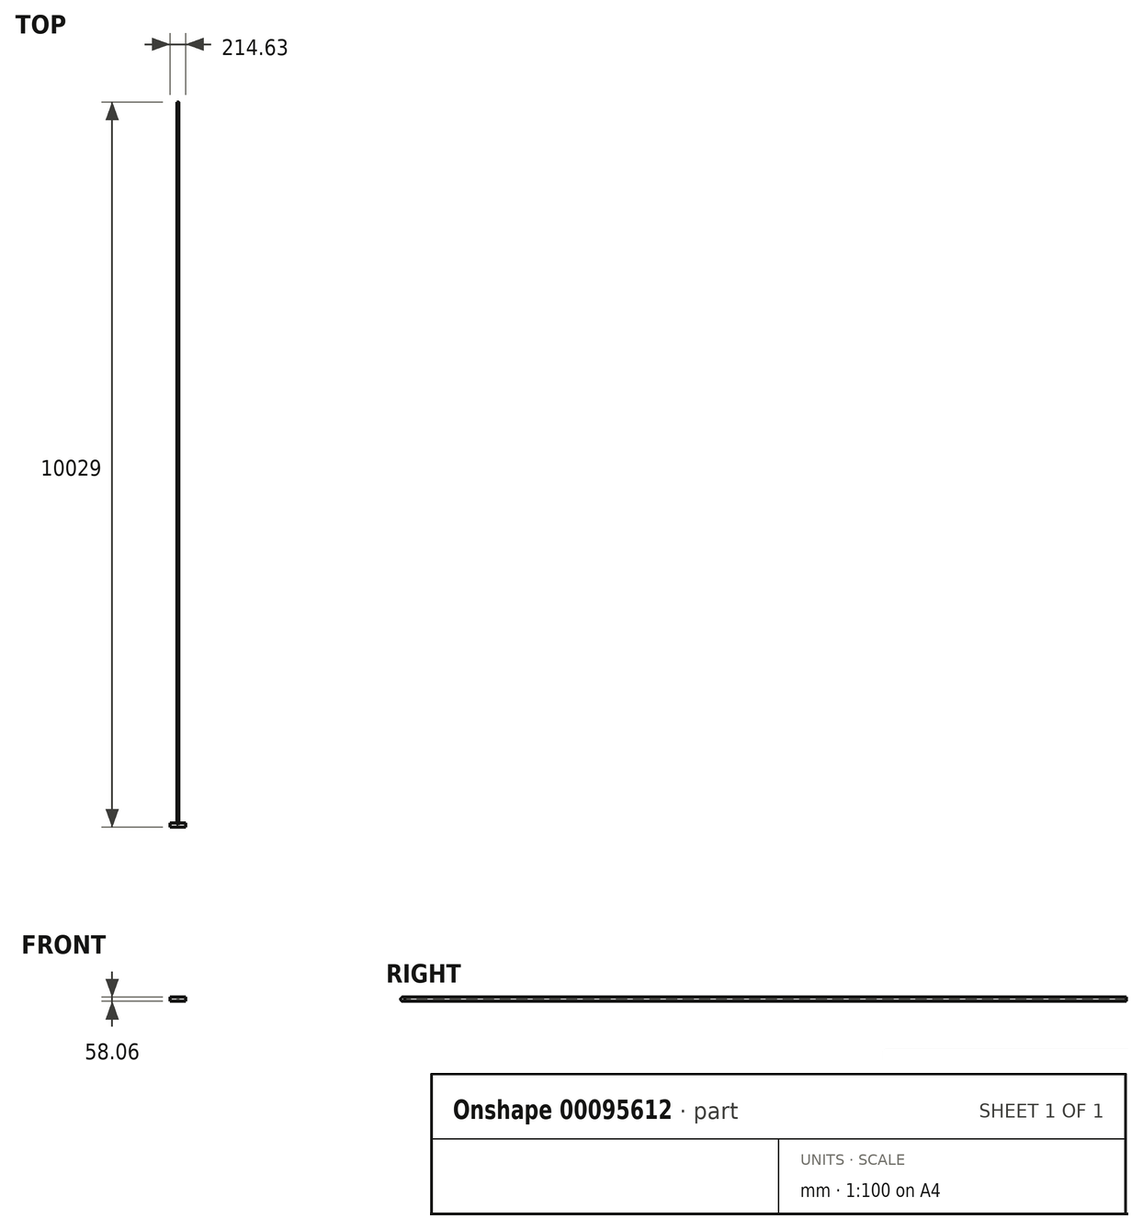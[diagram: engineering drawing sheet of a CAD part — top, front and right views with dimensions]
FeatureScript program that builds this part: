
annotation { "Feature Type Name" : "Feature", "Feature Type Description" : "" }
export const myFeature = defineFeature(function(context is Context, id is Id, definition is map)
    precondition{}
    {
        {
            var Q0;
            Q0=qCreatedBy(makeId("Right.planeOp"),FACE);
            var sketch = newSketch(context, id + "F0", { "sketchPlane" : qUnion([Q0])});
            skCircle(sketch, "E0", {"center": v(0, 0) * mm, "radius": 29.03 * mm});
            skSolve(sketch);
        }
        {
            var Q0;
            Q0=makeQuery(id+"F0.imprint","IMPRINT",FACE,{"disambiguationData":[TD([[makeQuery(id+"F0.imprint","IMPRINT",EDGE,{"derivedFrom":sQuery(id+"F0.wireOp",EDGE,"E0")}),1.0]])]});
            extrude(context, id + "F1", {"entities" : qUnion([Q0]), "depth" : 214.63 * mm});
        }
        {
            var Q0;
            Q0=qCreatedBy(makeId("Front.planeOp"),FACE);
            var sketch = newSketch(context, id + "F2", { "sketchPlane" : qUnion([Q0])});
            skArc(sketch, "E1", {"start": v(82.72, -29.36) * mm, "mid": v(86.37, 0) * mm, "end": v(83.92, 29.5) * mm});
            skArc(sketch, "E2", {"start": v(88.72, -28.76) * mm, "mid": v(90.68, -0.5) * mm, "end": v(84.35, 27.12) * mm});
            skArc(sketch, "E3", {"start": v(94.13, -28.16) * mm, "mid": v(113.33, -0.43) * mm, "end": v(94.73, 27.7) * mm});
            skArc(sketch, "E4", {"start": v(113.33, 28.3) * mm, "mid": v(108.51, 2.17) * mm, "end": v(113.33, -23.95) * mm});
            skPoint(sketch, "E4.startSnap0", {"position": v(113.33, -0.43) * mm});
            skPoint(sketch, "E4.endSnap0", {"position": v(113.33, -0.43) * mm});
            skArc(sketch, "E5", {"start": v(101.59, -23.95) * mm, "mid": v(104.19, 2.11) * mm, "end": v(104.94, 28.3) * mm});
            skArc(sketch, "E6", {"start": v(90.68, -23.95) * mm, "mid": v(95.93, 2.03) * mm, "end": v(89.32, 27.7) * mm});
            skPoint(sketch, "E6.startSnap0", {"position": v(90.68, -0.5) * mm});
            skArc(sketch, "E7", {"start": v(101.59, -23.95) * mm, "mid": v(103.38, 2.57) * mm, "end": v(94.73, 27.7) * mm});
            skArc(sketch, "E8", {"start": v(104.91, 20.76) * mm, "mid": v(99.73, -3.36) * mm, "end": v(113.33, -23.95) * mm});
            skArc(sketch, "E9", {"start": v(113.33, -23.95) * mm, "mid": v(118.79, 2.17) * mm, "end": v(113.33, 28.3) * mm});
            skArc(sketch, "E10", {"start": v(113.33, -23.95) * mm, "mid": v(115.54, 3.2) * mm, "end": v(104.94, 28.3) * mm});
            skArc(sketch, "E11", {"start": v(101.59, -23.95) * mm, "mid": v(109.07, 1.99) * mm, "end": v(95.93, 25.57) * mm});
            skPoint(sketch, "E11.endSnap0", {"position": v(95.93, 2.03) * mm});
            skArc(sketch, "E12", {"start": v(103.38, 2.57) * mm, "mid": v(94.17, -16.02) * mm, "end": v(113.33, -23.95) * mm});
            skSolve(sketch);
        }
        {
            var Q0;
            Q0 = qSketchRegion(id + "F2", true);
            extrude(context, id + "F3", {"entities" : qUnion([Q0]), "operationType" : NewBodyOperationType.ADD, "oppositeDirection" : true, "depth" : 10000 * mm});
        }
    });
